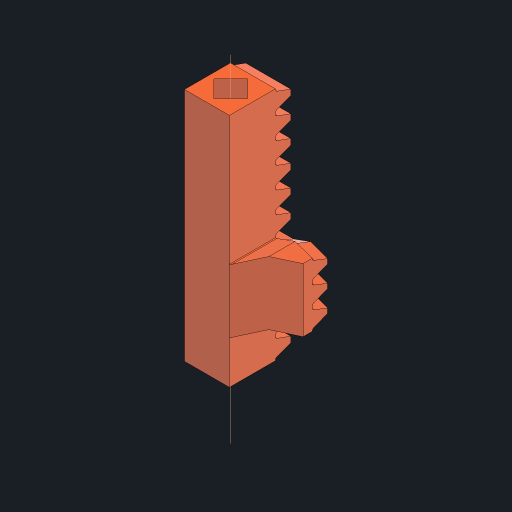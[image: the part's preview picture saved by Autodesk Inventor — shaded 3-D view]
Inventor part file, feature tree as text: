
AUTODESK INVENTOR PART (.ipt)
format: ipt  version: 2023.2 (Build 272271030, 271C)  size: 652,288 bytes
history: native  units: mm
features: sketch x5, projected_geometry x4, extrude x3, sweep x1, pattern_linear x1, other x1, chamfer x1
ambient origin geometry x8: Origin, YZ Plane, XZ Plane, XY Plane, X Axis, Y Axis, Z Axis, Center Point
bodies: Solid1 (feature_tree)
feature tree (16):
  extrude  "Extrusion1"  Depth=34.557519mm
  sweep  "Sweep1"
  pattern_linear  "Rectangular Pattern1"  Spacing1=0.38mm  [1 undecoded]
  sketch  "Sketch4"  dims[d6=1.570796mm]
  extrude  "Extrusion8"  Depth=6.6mm
  other  "Work Axis1"
  chamfer  "Chamfer2"  Distance=5.0mm
  extrude  "Extrusion11"  Depth=6.6mm
  sketch  "Sketch1"  dims[d0=12.0mm d1=34.557519mm]
  sketch  "Sketch2"  dims[d2=9.0mm d3=0.0mm d4=1.0mm]
  projected_geometry  "Projected Loop1"
  sketch  "Sketch3"  dims[d5=1.25mm]
  projected_geometry  "Projected Loop2"
  sketch  "Sketch11"  dims[d7=12.217305mm d17=0.38mm d27=7.0mm d28=5.0mm d29=3.490659mm d30=0.0mm d31=0.0mm d32=120.0mm d34=3.141593mm d56=0.0mm d57=0.0mm d60=3.5mm d61=3.3mm d62=5.5mm d64=5.4mm d65=2.0mm d66=45.0deg d71=6.6mm d72=0.0mm d73=0.0mm d43=0.5mm d44=0.872665mm d45=0.5mm d46=0.872665mm]
  projected_geometry  "Projected Loop24"
  projected_geometry  "Projected Loop25"
note: 1 required parameter value undecoded (feature->parameter linkage not recoverable at this tier; creation-order binding heuristic only, values carry confidence <= 0.55)
